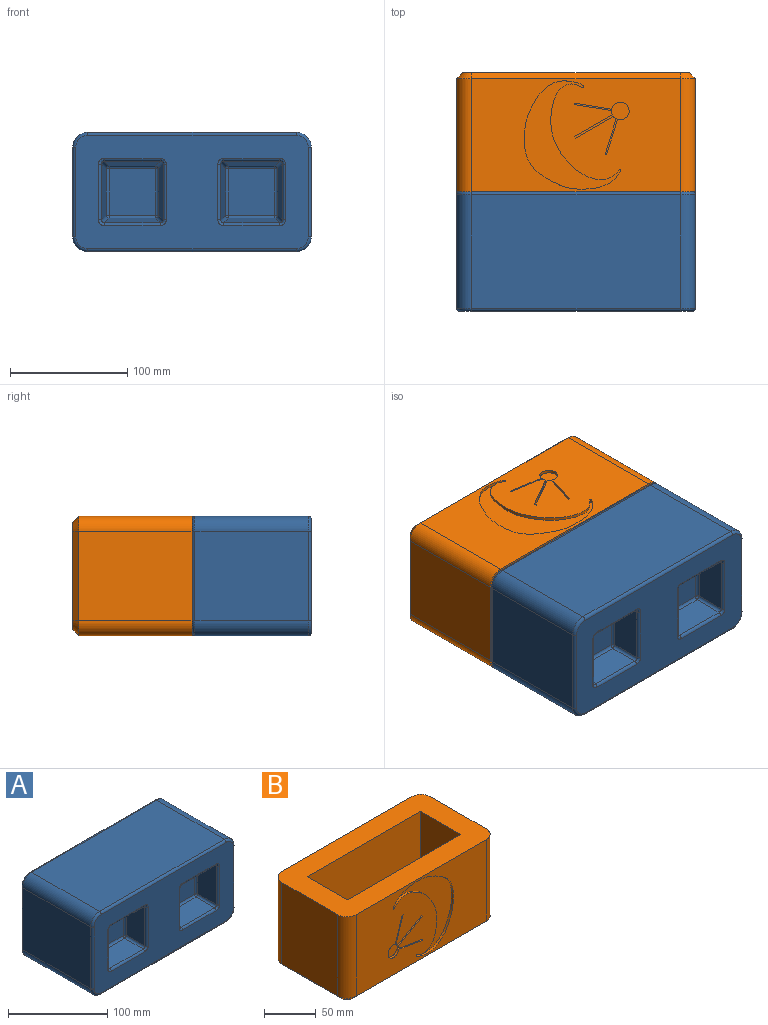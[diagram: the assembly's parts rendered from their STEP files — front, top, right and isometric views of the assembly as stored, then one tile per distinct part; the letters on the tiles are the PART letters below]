
ASSEMBLY  parts=2 mates=1
PART A: 196 faces, bbox 205.4x127.2x103.8 mm
  f0: bspline ~3.55x3.2mm, area 9.5mm2, adj f8,f130,f132,f133
  f1: bspline ~3.55x3.2mm, area 9.5mm2, adj f8,f82,f129,f131
  f2: bspline ~3.55x3.2mm, area 9.5mm2, adj f8,f122,f124,f125
  f3: bspline ~3.55x3.2mm, area 9.5mm2, adj f8,f70,f121,f123
  f4: bspline ~3.55x3.2mm, area 9.5mm2, adj f8,f84,f87,f88
  f5: bspline ~3.55x3.2mm, area 9.5mm2, adj f8,f82,f83,f86
  f6: bspline ~3.55x3.2mm, area 9.5mm2, adj f8,f72,f75,f76
  f7: bspline ~3.55x3.2mm, area 9.5mm2, adj f8,f70,f71,f74
  f8: plane 198.14x96.54mm, normal (0,1,0), area 13012.7mm2, adj f0,f1,f2,f3,f4,f5,f6,f7
  f9: plane 96.52x76.2mm, normal (1,0,0), area 7354.8mm2, adj f29,f31,f40,f94
  f10: plane 177.8x96.52mm, normal (0,0,-1), area 17161.3mm2, adj f29,f30,f33,f37
  f11: plane 96.52x76.2mm, normal (-1,0,0), area 7354.8mm2, adj f30,f34,f38,f95
  f12: plane 198.27x96.67mm, normal (0,-1,0), area 12440.4mm2, adj f36,f37,f38,f39,f40,f46,f47,f49
  f13: plane 45.06x21.2mm, normal (0.98,0.17,0), area 889.6mm2, adj f77,f82,f83,f129
  f14: plane 45.06x21.2mm, normal (0,0.17,-0.98), area 889.6mm2, adj f78,f83,f84,f88
  f15: plane 45.06x21.2mm, normal (-0.98,0.17,0), area 889.6mm2, adj f79,f84,f85,f130
  f16: plane 37.58x37.58mm, normal (0,1,0), area 1412.3mm2, adj f77,f78,f79,f126
  f17: plane 45.06x21.2mm, normal (0.98,0.17,0), area 889.6mm2, adj f65,f70,f71,f121
  f18: plane 45.06x21.2mm, normal (0,0.17,-0.98), area 889.6mm2, adj f66,f71,f72,f76
  f19: plane 45.06x21.2mm, normal (-0.98,0.17,0), area 889.6mm2, adj f67,f72,f73,f122
  f20: plane 37.58x37.58mm, normal (0,1,0), area 1412.3mm2, adj f65,f66,f67,f118
  f21: plane 47.6x22.47mm, normal (-0.98,-0.17,0), area 995.7mm2, adj f45,f50,f52,f108
  f22: plane 47.6x22.47mm, normal (0,-0.17,0.98), area 995.7mm2, adj f43,f44,f49,f50
  f23: plane 47.6x22.47mm, normal (0.98,-0.17,0), area 995.7mm2, adj f41,f43,f46,f103
  f24: plane 39.67x39.67mm, normal (0,-1,0), area 1573.9mm2, adj f41,f44,f45,f104
  f25: plane 47.6x22.47mm, normal (-0.98,-0.17,0), area 995.7mm2, adj f55,f60,f61,f114
  f26: plane 47.6x22.47mm, normal (0,-0.17,0.98), area 995.7mm2, adj f54,f59,f60,f64
  f27: plane 47.6x22.47mm, normal (0.98,-0.17,0), area 995.7mm2, adj f53,f58,f59,f113
  f28: plane 39.67x39.67mm, normal (0,-1,0), area 1573.9mm2, adj f53,f54,f55,f110
  f29: cylinder r=12.7mm len=96.52mm, axis (0,-1,0), area 1925.5mm2, adj f9,f10,f32,f39
  f30: cylinder r=12.7mm len=96.52mm, axis (0,-1,0), area 1925.5mm2, adj f10,f11,f35,f36
  f31: cylinder r=2.54mm len=76.2mm, axis (0,0,-1), area 304mm2, adj f8,f9,f32,f96
  f32: torus R=10.16mm, axis (0,-1,0), area 73.8mm2, adj f8,f29,f31,f33
  f33: cylinder r=2.54mm len=177.8mm, axis (-1,0,0), area 709.4mm2, adj f8,f10,f32,f35
  f34: cylinder r=2.54mm len=76.2mm, axis (0,0,1), area 304mm2, adj f8,f11,f35,f98
  f35: torus R=10.16mm, axis (0,-1,0), area 73.8mm2, adj f8,f30,f33,f34
  f36: torus R=10.16mm, axis (0,-1,0), area 73.8mm2, adj f12,f30,f37,f38
  f37: cylinder r=2.54mm len=177.8mm, axis (1,0,0), area 709.4mm2, adj f10,f12,f36,f39
  f38: cylinder r=2.54mm len=76.2mm, axis (0,0,-1), area 304mm2, adj f11,f12,f36,f99
  f39: torus R=10.16mm, axis (0,-1,0), area 73.8mm2, adj f12,f29,f37,f40
  f40: cylinder r=2.54mm len=76.2mm, axis (0,0,1), area 304mm2, adj f9,f12,f39,f101
  f41: cylinder r=2.54mm len=39.67mm, axis (0,0,-1), area 140.7mm2, adj f23,f24,f42,f102
  f42: sphere r=2.54mm, area 8.4mm2, adj f41,f43,f44
  f43: cylinder r=2.54mm len=22.99mm, axis (0.17,0.97,0.17), area 91.6mm2, adj f22,f23,f42,f47
  f44: cylinder r=2.54mm len=39.67mm, axis (1,0,0), area 140.7mm2, adj f22,f24,f42,f48
  f45: cylinder r=2.54mm len=39.67mm, axis (0,0,1), area 140.7mm2, adj f21,f24,f48,f106
  f46: cylinder r=2.54mm len=47.6mm, axis (0,0,1), area 168.8mm2, adj f12,f23,f47,f105
  f47: bspline ~5x5mm, area 19.1mm2, adj f12,f43,f46,f49
  f48: sphere r=2.54mm, area 7.9mm2, adj f44,f45,f50
  f49: cylinder r=2.54mm len=47.6mm, axis (-1,0,0), area 168.8mm2, adj f12,f22,f47,f51
  f50: cylinder r=2.54mm len=22.99mm, axis (-0.17,0.97,0.17), area 91.6mm2, adj f21,f22,f48,f51
  f51: bspline ~5x5mm, area 19.1mm2, adj f12,f49,f50,f52
  f52: cylinder r=2.54mm len=47.6mm, axis (0,0,-1), area 168.8mm2, adj f12,f21,f51,f109
  f53: cylinder r=2.54mm len=39.67mm, axis (0,0,-1), area 140.7mm2, adj f27,f28,f56,f111
  f54: cylinder r=2.54mm len=39.67mm, axis (1,0,0), area 140.7mm2, adj f26,f28,f56,f57
  f55: cylinder r=2.54mm len=39.67mm, axis (0,0,1), area 140.7mm2, adj f25,f28,f57,f112
  f56: sphere r=2.54mm, area 8.4mm2, adj f53,f54,f59
  f57: sphere r=2.54mm, area 7.9mm2, adj f54,f55,f60
  f58: cylinder r=2.54mm len=47.6mm, axis (0,0,1), area 168.8mm2, adj f12,f27,f62,f115
  f59: cylinder r=2.54mm len=22.99mm, axis (0.17,0.97,0.17), area 91.6mm2, adj f26,f27,f56,f62
  f60: cylinder r=2.54mm len=22.99mm, axis (-0.17,0.97,0.17), area 91.6mm2, adj f25,f26,f57,f63
  f61: cylinder r=2.54mm len=47.6mm, axis (0,0,-1), area 168.8mm2, adj f12,f25,f63,f116
  f62: bspline ~5x5mm, area 19.1mm2, adj f12,f58,f59,f64
  f63: bspline ~5x5mm, area 19.1mm2, adj f12,f60,f61,f64
  f64: cylinder r=2.54mm len=47.6mm, axis (-1,0,0), area 168.8mm2, adj f12,f26,f62,f63
  f65: cylinder r=2.54mm len=37.58mm, axis (0,0,1), area 133.3mm2, adj f17,f20,f68,f119
  f66: cylinder r=2.54mm len=37.58mm, axis (1,0,0), area 133.3mm2, adj f18,f20,f68,f69
  f67: cylinder r=2.54mm len=37.58mm, axis (0,0,-1), area 133.3mm2, adj f19,f20,f69,f120
  f68: sphere r=2.54mm, area 7.9mm2, adj f65,f66,f71
  f69: sphere r=2.54mm, area 8.4mm2, adj f66,f67,f72
  f70: cylinder r=2.54mm len=45.06mm, axis (0,0,-1), area 159.8mm2, adj f3,f7,f8,f17
  f71: cylinder r=2.54mm len=21.72mm, axis (0.17,-0.97,-0.17), area 86.2mm2, adj f7,f17,f18,f68,f74
  f72: cylinder r=2.54mm len=21.72mm, axis (-0.17,-0.97,-0.17), area 86.2mm2, adj f6,f18,f19,f69,f75
  f73: cylinder r=2.54mm len=45.06mm, axis (0,0,1), area 159.8mm2, adj f8,f19,f75,f124
  f74: bspline ~3.55x3.2mm, area 9.5mm2, adj f7,f8,f71,f76
  f75: bspline ~3.55x3.2mm, area 9.5mm2, adj f6,f8,f72,f73
  f76: cylinder r=2.54mm len=45.06mm, axis (-1,0,0), area 159.8mm2, adj f6,f8,f18,f74
  f77: cylinder r=2.54mm len=37.58mm, axis (0,0,1), area 133.3mm2, adj f13,f16,f80,f127
  f78: cylinder r=2.54mm len=37.58mm, axis (1,0,0), area 133.3mm2, adj f14,f16,f80,f81
  f79: cylinder r=2.54mm len=37.58mm, axis (0,0,-1), area 133.3mm2, adj f15,f16,f81,f128
  f80: sphere r=2.54mm, area 7.9mm2, adj f77,f78,f83
  f81: sphere r=2.54mm, area 8.4mm2, adj f78,f79,f84
  f82: cylinder r=2.54mm len=45.06mm, axis (0,0,-1), area 159.8mm2, adj f1,f5,f8,f13
  f83: cylinder r=2.54mm len=21.72mm, axis (0.17,-0.97,-0.17), area 86.2mm2, adj f5,f13,f14,f80,f86
  f84: cylinder r=2.54mm len=21.72mm, axis (-0.17,-0.97,-0.17), area 86.2mm2, adj f4,f14,f15,f81,f87
  f85: cylinder r=2.54mm len=45.06mm, axis (0,0,1), area 159.8mm2, adj f8,f15,f87,f132
  f86: bspline ~3.55x3.2mm, area 9.5mm2, adj f5,f8,f83,f88
  f87: bspline ~3.55x3.2mm, area 9.5mm2, adj f4,f8,f84,f85
  f88: cylinder r=2.54mm len=45.06mm, axis (-1,0,0), area 159.8mm2, adj f4,f8,f14,f86
  f89: plane 177.8x96.52mm, normal (0,0,1), area 17161.3mm2, adj f94,f95,f97,f100
  f90: plane 45.06x21.2mm, normal (0,0.17,0.98), area 889.6mm2, adj f126,f129,f130,f133
  f91: plane 45.06x21.2mm, normal (0,0.17,0.98), area 889.6mm2, adj f118,f121,f122,f125
  f92: plane 47.6x22.47mm, normal (0,-0.17,-0.98), area 995.7mm2, adj f103,f104,f107,f108
  f93: plane 47.6x22.47mm, normal (0,-0.17,-0.98), area 995.7mm2, adj f110,f113,f114,f117
  f94: cylinder r=12.7mm len=96.52mm, axis (0,-1,0), area 1925.5mm2, adj f9,f89,f96,f101
  f95: cylinder r=12.7mm len=96.52mm, axis (0,-1,0), area 1925.5mm2, adj f11,f89,f98,f99
  f96: torus R=10.16mm, axis (0,-1,0), area 73.8mm2, adj f8,f31,f94,f97
  f97: cylinder r=2.54mm len=177.8mm, axis (-1,0,0), area 709.4mm2, adj f8,f89,f96,f98
  f98: torus R=10.16mm, axis (0,-1,0), area 73.8mm2, adj f8,f34,f95,f97
  f99: torus R=10.16mm, axis (0,-1,0), area 73.8mm2, adj f12,f38,f95,f100
  f100: cylinder r=2.54mm len=177.8mm, axis (1,0,0), area 709.4mm2, adj f12,f89,f99,f101
  f101: torus R=10.16mm, axis (0,-1,0), area 73.8mm2, adj f12,f40,f94,f100
  f102: sphere r=2.54mm, area 8.4mm2, adj f41,f103,f104
  f103: cylinder r=2.54mm len=22.99mm, axis (0.17,0.97,-0.17), area 91.6mm2, adj f23,f92,f102,f105
  f104: cylinder r=2.54mm len=39.67mm, axis (1,0,0), area 140.7mm2, adj f24,f92,f102,f106
  f105: bspline ~5x5mm, area 19.1mm2, adj f12,f46,f103,f107
  f106: sphere r=2.54mm, area 7.9mm2, adj f45,f104,f108
  f107: cylinder r=2.54mm len=47.6mm, axis (-1,0,0), area 168.8mm2, adj f12,f92,f105,f109
  f108: cylinder r=2.54mm len=22.99mm, axis (-0.17,0.97,-0.17), area 91.6mm2, adj f21,f92,f106,f109
  f109: bspline ~5x5mm, area 19.1mm2, adj f12,f52,f107,f108
  f110: cylinder r=2.54mm len=39.67mm, axis (1,0,0), area 140.7mm2, adj f28,f93,f111,f112
  f111: sphere r=2.54mm, area 8.4mm2, adj f53,f110,f113
  f112: sphere r=2.54mm, area 7.9mm2, adj f55,f110,f114
  f113: cylinder r=2.54mm len=22.99mm, axis (0.17,0.97,-0.17), area 91.6mm2, adj f27,f93,f111,f115
  f114: cylinder r=2.54mm len=22.99mm, axis (-0.17,0.97,-0.17), area 91.6mm2, adj f25,f93,f112,f116
  f115: bspline ~5x5mm, area 19.1mm2, adj f12,f58,f113,f117
  f116: bspline ~5x5mm, area 19.1mm2, adj f12,f61,f114,f117
  f117: cylinder r=2.54mm len=47.6mm, axis (-1,0,0), area 168.8mm2, adj f12,f93,f115,f116
  f118: cylinder r=2.54mm len=37.58mm, axis (1,0,0), area 133.3mm2, adj f20,f91,f119,f120
  f119: sphere r=2.54mm, area 7.9mm2, adj f65,f118,f121
  f120: sphere r=2.54mm, area 8.4mm2, adj f67,f118,f122
  f121: cylinder r=2.54mm len=21.72mm, axis (0.17,-0.97,0.17), area 86.2mm2, adj f3,f17,f91,f119,f123
  f122: cylinder r=2.54mm len=21.72mm, axis (-0.17,-0.97,0.17), area 86.2mm2, adj f2,f19,f91,f120,f124
  f123: bspline ~3.55x3.2mm, area 9.5mm2, adj f3,f8,f121,f125
  f124: bspline ~3.55x3.2mm, area 9.5mm2, adj f2,f8,f73,f122
  f125: cylinder r=2.54mm len=45.06mm, axis (-1,0,0), area 159.8mm2, adj f2,f8,f91,f123
  f126: cylinder r=2.54mm len=37.58mm, axis (1,0,0), area 133.3mm2, adj f16,f90,f127,f128
  f127: sphere r=2.54mm, area 7.9mm2, adj f77,f126,f129
  f128: sphere r=2.54mm, area 8.4mm2, adj f79,f126,f130
  f129: cylinder r=2.54mm len=21.72mm, axis (0.17,-0.97,0.17), area 86.2mm2, adj f1,f13,f90,f127,f131
  f130: cylinder r=2.54mm len=21.72mm, axis (-0.17,-0.97,0.17), area 86.2mm2, adj f0,f15,f90,f128,f132
  f131: bspline ~3.55x3.2mm, area 9.5mm2, adj f1,f8,f129,f133
  f132: bspline ~3.55x3.2mm, area 9.5mm2, adj f0,f8,f85,f130
  f133: cylinder r=2.54mm len=45.06mm, axis (-1,0,0), area 159.8mm2, adj f0,f8,f90,f131
  f134: sphere r=5.08mm, area 31.7mm2, adj f135,f145,f194
  f135: cylinder r=5.08mm len=39.67mm, axis (1,0,0), area 281.4mm2, adj f134,f136,f144,f193
  f136: sphere r=5.08mm, area 31.7mm2, adj f135,f143,f192
  f137: sphere r=5.08mm, area 31.7mm2, adj f138,f142,f189
  f138: cylinder r=5.08mm len=39.67mm, axis (1,0,0), area 281.4mm2, adj f137,f139,f141,f188
  f139: sphere r=5.08mm, area 31.7mm2, adj f138,f140,f187
  f140: cylinder r=5.08mm len=23.17mm, axis (0.17,0.97,-0.17), area 183.1mm2, adj f139,f141,f185,f186
  f141: plane 47.6x22.47mm, normal (0,0.17,0.98), area 995.7mm2, adj f138,f140,f142,f185
  f142: cylinder r=5.08mm len=23.17mm, axis (-0.17,0.97,-0.17), area 183.1mm2, adj f137,f141,f185,f190
  f143: cylinder r=5.08mm len=23.17mm, axis (0.17,0.97,-0.17), area 183.1mm2, adj f136,f144,f185,f191
  f144: plane 47.6x22.47mm, normal (0,0.17,0.98), area 995.7mm2, adj f135,f143,f145,f185
  f145: cylinder r=5.08mm len=23.17mm, axis (-0.17,0.97,-0.17), area 183.1mm2, adj f134,f144,f185,f195
  f146: plane 45.06x21.2mm, normal (0,-0.17,-0.98), area 889.6mm2, adj f151,f180,f181,f182
  f147: plane 45.06x21.2mm, normal (0,-0.17,-0.98), area 889.6mm2, adj f150,f175,f176,f177
  f148: cylinder r=10.16mm len=96.52mm, axis (0,-1,0), area 1540.4mm2, adj f149,f173,f184,f185
  f149: plane 177.8x96.52mm, normal (0,0,-1), area 17161.3mm2, adj f148,f152,f173,f185
  f150: cylinder r=5.08mm len=55.06mm, axis (-1,0,0), area 347.9mm2, adj f147,f173,f174,f178
  f151: cylinder r=5.08mm len=55.06mm, axis (-1,0,0), area 347.9mm2, adj f146,f173,f179,f183
  f152: cylinder r=10.16mm len=96.52mm, axis (0,-1,0), area 1540.4mm2, adj f149,f172,f173,f185
  f153: sphere r=5.08mm, area 31.7mm2, adj f154,f159,f194
  f154: cylinder r=5.08mm len=39.67mm, axis (1,0,0), area 281.4mm2, adj f153,f155,f160,f193
  f155: sphere r=5.08mm, area 31.7mm2, adj f154,f161,f192
  f156: sphere r=5.08mm, area 31.7mm2, adj f157,f162,f189
  f157: cylinder r=5.08mm len=39.67mm, axis (1,0,0), area 281.4mm2, adj f156,f158,f163,f188
  f158: sphere r=5.08mm, area 31.7mm2, adj f157,f164,f187
  f159: cylinder r=5.08mm len=23.17mm, axis (-0.17,0.97,0.17), area 183.1mm2, adj f153,f160,f185,f195
  f160: plane 47.6x22.47mm, normal (0,0.17,-0.98), area 995.7mm2, adj f154,f159,f161,f185
  f161: cylinder r=5.08mm len=23.17mm, axis (0.17,0.97,0.17), area 183.1mm2, adj f155,f160,f185,f191
  f162: cylinder r=5.08mm len=23.17mm, axis (-0.17,0.97,0.17), area 183.1mm2, adj f156,f163,f185,f190
  f163: plane 47.6x22.47mm, normal (0,0.17,-0.98), area 995.7mm2, adj f157,f162,f164,f185
  f164: cylinder r=5.08mm len=23.17mm, axis (0.17,0.97,0.17), area 183.1mm2, adj f158,f163,f185,f186
  f165: plane 45.06x21.2mm, normal (0,-0.17,0.98), area 889.6mm2, adj f167,f180,f181,f182
  f166: plane 45.06x21.2mm, normal (0,-0.17,0.98), area 889.6mm2, adj f168,f175,f176,f177
  f167: cylinder r=5.08mm len=55.06mm, axis (-1,0,0), area 347.9mm2, adj f165,f173,f179,f183
  f168: cylinder r=5.08mm len=55.06mm, axis (-1,0,0), area 347.9mm2, adj f166,f173,f174,f178
  f169: plane 177.8x96.52mm, normal (0,0,1), area 17161.3mm2, adj f170,f171,f173,f185
  f170: cylinder r=10.16mm len=96.52mm, axis (0,-1,0), area 1540.4mm2, adj f169,f173,f184,f185
  f171: cylinder r=10.16mm len=96.52mm, axis (0,-1,0), area 1540.4mm2, adj f169,f172,f173,f185
  f172: plane 96.52x76.2mm, normal (-1,0,0), area 7354.8mm2, adj f152,f171,f173,f185
  f173: plane 198.12x96.52mm, normal (0,-1,0), area 12970.1mm2, adj f148,f149,f150,f151,f152,f167,f168,f169
  f174: cylinder r=5.08mm len=55.06mm, axis (0,0,-1), area 347.9mm2, adj f150,f168,f173,f175
  f175: plane 45.06x21.2mm, normal (-0.98,-0.17,0), area 889.6mm2, adj f147,f166,f174,f176
  f176: plane 37.58x37.58mm, normal (0,-1,0), area 1412.3mm2, adj f147,f166,f175,f177
  f177: plane 45.06x21.2mm, normal (0.98,-0.17,0), area 889.6mm2, adj f147,f166,f176,f178
  f178: cylinder r=5.08mm len=55.06mm, axis (0,0,1), area 347.9mm2, adj f150,f168,f173,f177
  f179: cylinder r=5.08mm len=55.06mm, axis (0,0,-1), area 347.9mm2, adj f151,f167,f173,f180
  f180: plane 45.06x21.2mm, normal (-0.98,-0.17,0), area 889.6mm2, adj f146,f165,f179,f181
  f181: plane 37.58x37.58mm, normal (0,-1,0), area 1412.3mm2, adj f146,f165,f180,f182
  f182: plane 45.06x21.2mm, normal (0.98,-0.17,0), area 889.6mm2, adj f146,f165,f181,f183
  f183: cylinder r=5.08mm len=55.06mm, axis (0,0,1), area 347.9mm2, adj f151,f167,f173,f182
  f184: plane 96.52x76.2mm, normal (1,0,0), area 7354.8mm2, adj f148,f170,f173,f185
  f185: plane 198.12x96.52mm, normal (0,1,0), area 12440.4mm2, adj f140,f141,f142,f143,f144,f145,f148,f149
  f186: plane 47.6x22.47mm, normal (-0.98,0.17,0), area 995.7mm2, adj f140,f164,f185,f187
  f187: cylinder r=5.08mm len=39.67mm, axis (0,0,-1), area 281.4mm2, adj f139,f158,f186,f188
  f188: plane 39.67x39.67mm, normal (0,1,0), area 1573.9mm2, adj f138,f157,f187,f189
  f189: cylinder r=5.08mm len=39.67mm, axis (0,0,1), area 281.4mm2, adj f137,f156,f188,f190
  f190: plane 47.6x22.47mm, normal (0.98,0.17,0), area 995.7mm2, adj f142,f162,f185,f189
  f191: plane 47.6x22.47mm, normal (-0.98,0.17,0), area 995.7mm2, adj f143,f161,f185,f192
  f192: cylinder r=5.08mm len=39.67mm, axis (0,0,-1), area 281.4mm2, adj f136,f155,f191,f193
  f193: plane 39.67x39.67mm, normal (0,1,0), area 1573.9mm2, adj f135,f154,f192,f194
  f194: cylinder r=5.08mm len=39.67mm, axis (0,0,1), area 281.4mm2, adj f134,f153,f193,f195
  f195: plane 47.6x22.47mm, normal (0.98,0.17,0), area 995.7mm2, adj f145,f159,f185,f194
PART B: 110 faces, bbox 203.2x101.6x101.6 mm
  f0: plane 177.8x96.52mm, normal (0,-1,0), area 14467mm2, adj f8,f10,f11,f87,f88,f89,f90,f91
  f1: plane 177.8x96.52mm, normal (0,1,0), area 13775.5mm2, adj f8,f12,f13,f23,f24,f25,f26,f27
  f2: plane 95.25x55mm, normal (1,0,0), area 5238.8mm2, adj f3,f7,f8,f86
  f3: plane 155x95.25mm, normal (0,-1,0), area 14763.7mm2, adj f2,f4,f8,f86
  f4: plane 95.25x55mm, normal (-1,0,0), area 5238.8mm2, adj f3,f7,f8,f86
  f5: plane 96.52x76.2mm, normal (-1,0,0), area 7354.8mm2, adj f8,f10,f13,f105
  f6: plane 96.52x76.2mm, normal (1,0,0), area 7354.8mm2, adj f8,f11,f12,f106
  f7: plane 155x95.25mm, normal (0,1,0), area 14763.7mm2, adj f2,f4,f8,f86
  f8: plane 203.2x101.6mm, normal (0,0,1), area 11981.7mm2, adj f0,f1,f2,f3,f4,f5,f6,f7
  f9: plane 193.04x91.44mm, normal (0,0,-1), area 17601.7mm2, adj f102,f103,f104,f105,f106,f107,f108,f109
  f10: cylinder r=12.7mm len=96.52mm, axis (0,0,1), area 1925.5mm2, adj f0,f5,f8,f107
  f11: cylinder r=12.7mm len=96.52mm, axis (0,0,-1), area 1925.5mm2, adj f0,f6,f8,f108
  f12: cylinder r=12.7mm len=96.52mm, axis (0,0,1), area 1925.5mm2, adj f1,f6,f8,f104
  f13: cylinder r=12.7mm len=96.52mm, axis (0,0,-1), area 1925.5mm2, adj f1,f5,f8,f103
  f14: extruded ~9.87x2.54mm, area 26.2mm2, adj f15,f33,f34,f85
  f15: plane 14.84x2.54mm, normal (1,0,0), area 37.7mm2, adj f14,f16,f34,f85
  f16: extruded ~9.92x2.54mm, area 26.3mm2, adj f15,f17,f34,f85
  f17: extruded ~6.9x3.33mm, area 20.3mm2, adj f16,f18,f34,f85
  f18: extruded ~6.87x3.35mm, area 20.2mm2, adj f17,f19,f34,f85
  f19: extruded ~9.91x2.54mm, area 26.3mm2, adj f18,f20,f34,f85
  f20: plane 14.84x2.54mm, normal (-1,0,0), area 37.7mm2, adj f19,f21,f34,f85
  f21: extruded ~9.87x2.54mm, area 26.2mm2, adj f20,f22,f34,f85
  f22: extruded ~6.84x3.32mm, area 20.1mm2, adj f21,f33,f34,f85
  f23: extruded ~14.84x4.31mm, area 40.1mm2, adj f1,f24,f32,f34
  f24: plane 11.99x2.54mm, normal (-1,0,0), area 30.5mm2, adj f1,f23,f25,f34
  f25: extruded ~14.84x4.34mm, area 40.1mm2, adj f1,f24,f26,f34
  f26: extruded ~11.81x5.2mm, area 33.9mm2, adj f1,f25,f27,f34
  f27: extruded ~11.74x5.2mm, area 33.8mm2, adj f1,f26,f28,f34
  f28: extruded ~14.84x4.31mm, area 40.1mm2, adj f1,f27,f29,f34
  f29: plane 11.99x2.54mm, normal (1,0,0), area 30.5mm2, adj f1,f28,f30,f34
  f30: extruded ~14.83x4.34mm, area 40mm2, adj f1,f29,f31,f34
  f31: extruded ~11.78x5.18mm, area 33.8mm2, adj f1,f30,f32,f34
  f32: extruded ~11.78x5.16mm, area 33.8mm2, adj f1,f23,f31,f34
  f33: extruded ~6.92x3.32mm, area 20.3mm2, adj f14,f22,f34,f85
  f34: plane 52.04x32.2mm, normal (0,1,0), area 762mm2, adj f14,f15,f16,f17,f18,f19,f20,f21
  f35: extruded ~19.33x12.39mm, area 58.6mm2, adj f1,f36,f47,f48
  f36: plane 5.38x2.54mm, normal (-1,0,0), area 13.7mm2, adj f1,f35,f37,f48
  f37: plane 34.18x2.54mm, normal (0,0,1), area 86.8mm2, adj f1,f36,f38,f48
  f38: plane 11.18x2.54mm, normal (1,0,0), area 28.4mm2, adj f1,f37,f39,f48
  f39: plane 5.83x2.54mm, normal (0,0,-1), area 14.8mm2, adj f1,f38,f40,f48
  f40: plane 5.8x2.54mm, normal (-1,0,-0.09), area 14.8mm2, adj f1,f39,f41,f48
  f41: plane 21.12x2.54mm, normal (0,0,-1), area 53.6mm2, adj f1,f40,f42,f48
  f42: extruded ~18.38x11.49mm, area 55.2mm2, adj f1,f41,f43,f48
  f43: extruded ~21.36x5.66mm, area 56.3mm2, adj f1,f42,f44,f48
  f44: plane 5.46x2.54mm, normal (0.99,0,0.1), area 13.9mm2, adj f1,f43,f45,f48
  f45: plane 6.84x2.54mm, normal (0,0,-1), area 17.4mm2, adj f1,f44,f46,f48
  f46: plane 5.46x2.54mm, normal (-0.99,0,-0.1), area 13.9mm2, adj f1,f45,f47,f48
  f47: extruded ~20.4x4.64mm, area 53.3mm2, adj f1,f35,f46,f48
  f48: plane 50.57x34.18mm, normal (0,1,0), area 514.4mm2, adj f35,f36,f37,f38,f39,f40,f41,f42
  f49: extruded ~19.33x12.39mm, area 58.6mm2, adj f1,f50,f61,f62
  f50: plane 5.38x2.54mm, normal (-1,0,0), area 13.7mm2, adj f1,f49,f51,f62
  f51: plane 34.18x2.54mm, normal (0,0,1), area 86.8mm2, adj f1,f50,f52,f62
  f52: plane 11.18x2.54mm, normal (1,0,0), area 28.4mm2, adj f1,f51,f53,f62
  f53: plane 5.83x2.54mm, normal (0,0,-1), area 14.8mm2, adj f1,f52,f54,f62
  f54: plane 5.8x2.54mm, normal (-1,0,-0.09), area 14.8mm2, adj f1,f53,f55,f62
  f55: plane 21.12x2.54mm, normal (0,0,-1), area 53.6mm2, adj f1,f54,f56,f62
  f56: extruded ~18.38x11.49mm, area 55.2mm2, adj f1,f55,f57,f62
  f57: extruded ~21.36x5.66mm, area 56.3mm2, adj f1,f56,f58,f62
  f58: plane 5.46x2.54mm, normal (0.99,0,0.1), area 13.9mm2, adj f1,f57,f59,f62
  f59: plane 6.84x2.54mm, normal (0,0,-1), area 17.4mm2, adj f1,f58,f60,f62
  f60: plane 5.46x2.54mm, normal (-0.99,0,-0.1), area 13.9mm2, adj f1,f59,f61,f62
  f61: extruded ~20.4x4.64mm, area 53.3mm2, adj f1,f49,f60,f62
  f62: plane 50.57x34.18mm, normal (0,1,0), area 514.4mm2, adj f49,f50,f51,f52,f53,f54,f55,f56
  f63: plane 7.81x2.54mm, normal (0.12,0,0.99), area 20mm2, adj f1,f64,f72,f73
  f64: plane 4.38x2.54mm, normal (1,0,0), area 11.1mm2, adj f1,f63,f65,f73
  f65: plane 22.44x2.54mm, normal (0,0,-1), area 57mm2, adj f1,f64,f66,f73
  f66: plane 4.38x2.54mm, normal (-1,0,0), area 11.1mm2, adj f1,f65,f67,f73
  f67: plane 7.78x2.54mm, normal (-0.12,0,0.99), area 19.9mm2, adj f1,f66,f68,f73
  f68: plane 45.22x2.54mm, normal (-1,0,0), area 114.9mm2, adj f1,f67,f69,f73
  f69: plane 14.79x3.19mm, normal (0.21,0,0.98), area 38.4mm2, adj f1,f68,f70,f73
  f70: plane 4.28x2.54mm, normal (1,0,0), area 10.9mm2, adj f1,f69,f71,f73
  f71: plane 7.95x2.54mm, normal (-0.02,0,-1), area 20.2mm2, adj f1,f70,f72,f73
  f72: plane 37.9x2.54mm, normal (1,0,0), area 96.3mm2, adj f1,f63,f71,f73
  f73: plane 50.57x22.57mm, normal (0,1,0), area 457.2mm2, adj f63,f64,f65,f66,f67,f68,f69,f70
  f74: plane 7.81x2.54mm, normal (0.12,0,0.99), area 20mm2, adj f1,f75,f83,f84
  f75: plane 4.38x2.54mm, normal (1,0,0), area 11.1mm2, adj f1,f74,f76,f84
  f76: plane 22.44x2.54mm, normal (0,0,-1), area 57mm2, adj f1,f75,f77,f84
  f77: plane 4.38x2.54mm, normal (-1,0,0), area 11.1mm2, adj f1,f76,f78,f84
  f78: plane 7.78x2.54mm, normal (-0.12,0,0.99), area 19.9mm2, adj f1,f77,f79,f84
  f79: plane 45.22x2.54mm, normal (-1,0,0), area 114.9mm2, adj f1,f78,f80,f84
  f80: plane 14.79x3.19mm, normal (0.21,0,0.98), area 38.4mm2, adj f1,f79,f81,f84
  f81: plane 4.28x2.54mm, normal (1,0,0), area 10.9mm2, adj f1,f80,f82,f84
  f82: plane 7.95x2.54mm, normal (-0.02,0,-1), area 20.2mm2, adj f1,f81,f83,f84
  f83: plane 37.9x2.54mm, normal (1,0,0), area 96.3mm2, adj f1,f74,f82,f84
  f84: plane 50.57x22.57mm, normal (0,1,0), area 457.2mm2, adj f74,f75,f76,f77,f78,f79,f80,f81
  f85: plane 41.29x18.5mm, normal (0,1,0), area 680.5mm2, adj f14,f15,f16,f17,f18,f19,f20,f21
  f86: plane 155x55mm, normal (0,0,1), area 8525mm2, adj f2,f3,f4,f7
  f87: plane 31.83x5.11mm, normal (-0.16,0,-0.99), area 81.9mm2, adj f0,f88,f98,f99
  f88: cylinder r=7.51mm len=3.37mm, axis (0,-1,0), area 8.8mm2, adj f0,f87,f89,f99
  f89: plane 32.43x18.75mm, normal (-0.5,0,0.87), area 95.2mm2, adj f0,f88,f90,f99
  f90: plane 2.54x1.52mm, normal (-0.87,0,-0.5), area 4.5mm2, adj f0,f89,f91,f99
  f91: plane 32.43x18.75mm, normal (0.5,0,-0.87), area 95.2mm2, adj f0,f90,f92,f99
  f92: cylinder r=7.51mm len=2.54mm, axis (0,-1,0), area 8.5mm2, adj f0,f91,f93,f99
  f93: plane 30.28x9.5mm, normal (-0.95,0,0.3), area 80.6mm2, adj f0,f92,f94,f99
  f94: plane 2.54x1.35mm, normal (0,0,-1), area 3.4mm2, adj f0,f93,f95,f99
  f95: plane 29.78x9.34mm, normal (0.95,0,-0.3), area 79.3mm2, adj f0,f94,f96,f99
  f96: cylinder r=7.51mm len=15.03mm, axis (0,-1,0), area 91.8mm2, adj f0,f95,f97,f99
  f97: plane 31.98x5.13mm, normal (0.16,0,0.99), area 82.3mm2, adj f0,f96,f98,f99
  f98: plane 2.54x1.2mm, normal (-1,0,0), area 3.1mm2, adj f0,f87,f97,f99
  f99: plane 46.84x44.44mm, normal (0,-1,0), area 322.1mm2, adj f87,f88,f89,f90,f91,f92,f93,f94
  f100: extruded ~92.01x81.71mm, area 845mm2, adj f0,f101
  f101: plane 92.76x82.49mm, normal (0,-1,0), area 2373.6mm2, adj f100
  f102: plane 177.8x5.08mm, normal (0,0.71,-0.71), area 1277.4mm2, adj f1,f9,f103,f104
  f103: cone r=7.62mm half-angle=45deg, axis (0,0,1), area 114.7mm2, adj f9,f13,f102,f105
  f104: cone r=7.62mm half-angle=45deg, axis (0,0,1), area 114.7mm2, adj f9,f12,f102,f106
  f105: plane 76.2x5.08mm, normal (-0.71,0,-0.71), area 547.4mm2, adj f5,f9,f103,f107
  f106: plane 76.2x5.08mm, normal (0.71,0,-0.71), area 547.4mm2, adj f6,f9,f104,f108
  f107: cone r=7.62mm half-angle=45deg, axis (0,0,1), area 114.7mm2, adj f9,f10,f105,f109
  f108: cone r=7.62mm half-angle=45deg, axis (0,0,1), area 114.7mm2, adj f9,f11,f106,f109
  f109: plane 177.8x5.08mm, normal (0,-0.71,-0.71), area 1277.4mm2, adj f0,f9,f107,f108
PLACE A t=(-71.55,42.52,-12.72)mm
PLACE B rot(axis=(0,-0.71,0.71),180deg) t=(30.05,245.72,38.08)mm
MATE fastened B.f8 <-> A.f8  axis (0,-1,0) through (-71.55,144.12,-12.72)mm
